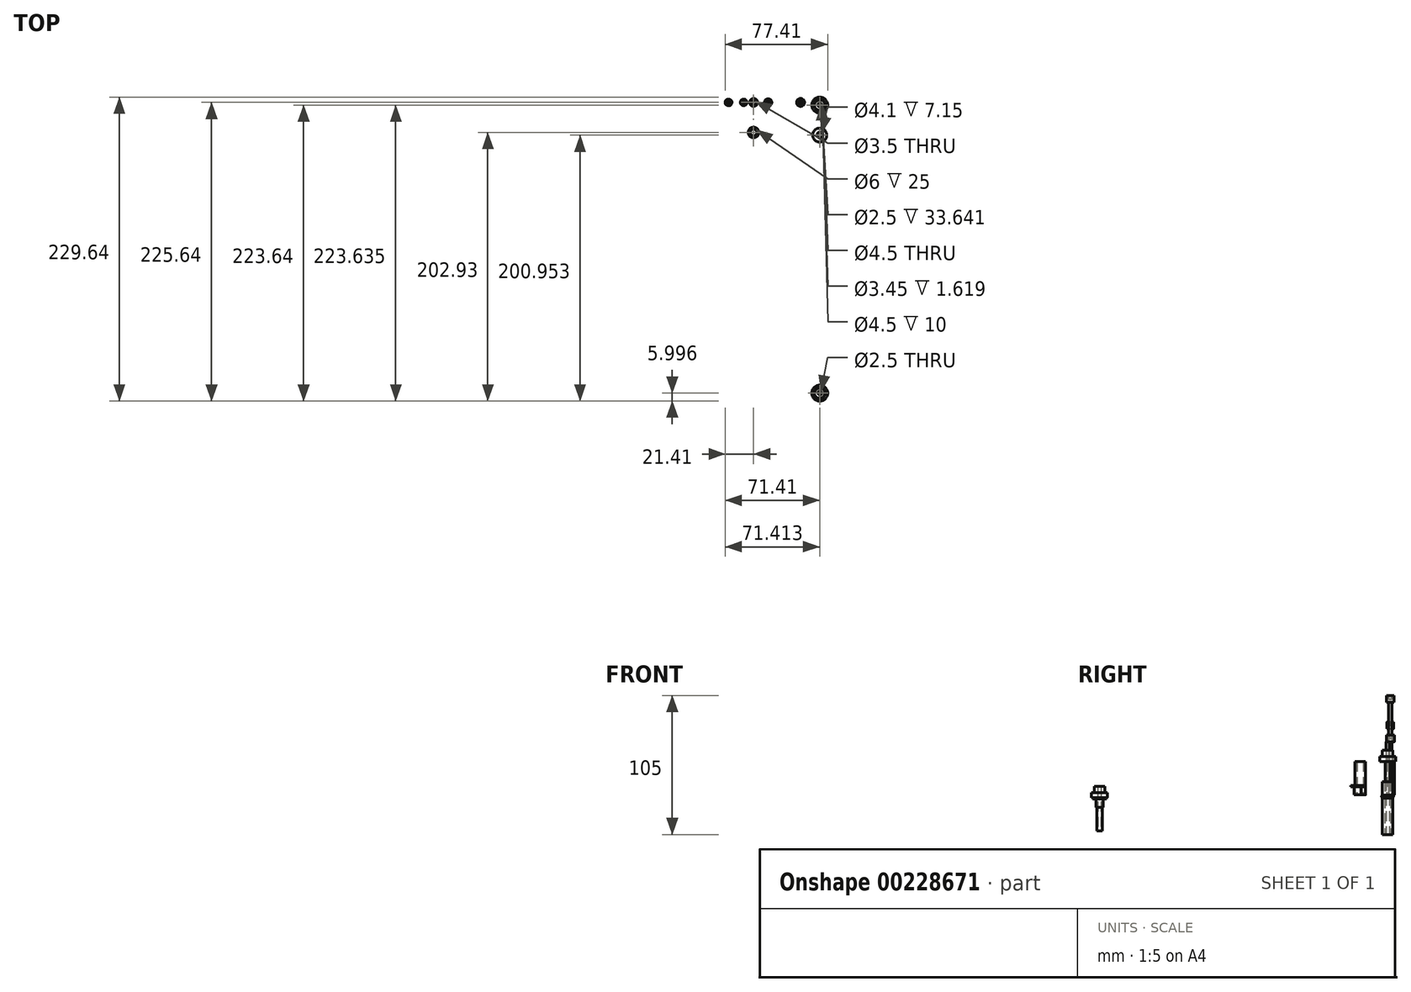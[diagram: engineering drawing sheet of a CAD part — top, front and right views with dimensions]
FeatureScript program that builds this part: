
annotation { "Feature Type Name" : "Feature", "Feature Type Description" : "" }
export const myFeature = defineFeature(function(context is Context, id is Id, definition is map)
    precondition{}
    {
        {
            var Q0;
            Q0=qCreatedBy(makeId("Top.planeOp"),FACE);
            var sketch = newSketch(context, id + "F0", { "sketchPlane" : qUnion([Q0])});
            skCircle(sketch, "E0", {"center": v(0, 0) * mm, "radius": 1.75 * mm});
            skCircle(sketch, "E1", {"center": v(0, 0) * mm, "radius": 3 * mm});
            skSolve(sketch);
        }
        {
            var Q0;
            Q0=makeQuery(id+"F0.imprint","IMPRINT",FACE,{"disambiguationData":[TD([[makeQuery(id+"F0.imprint","IMPRINT",EDGE,{"derivedFrom":sQuery(id+"F0.wireOp",EDGE,"E0")}),-1.0]])]});
            extrude(context, id + "F1", {"entities" : qUnion([Q0]), "depth" : 25 * mm});
        }
        {
            var Q0;
            Q0=qCreatedBy(makeId("Top.planeOp"),FACE);
            var sketch = newSketch(context, id + "F2", { "sketchPlane" : qUnion([Q0])});
            skCircle(sketch, "E2", {"center": v(-18.9, 0) * mm, "radius": 1 * mm});
            skSolve(sketch);
        }
        {
            var Q0;
            Q0=makeQuery(id+"F2.imprint","IMPRINT",FACE,{"disambiguationData":[TD([[makeQuery(id+"F2.imprint","IMPRINT",EDGE,{"derivedFrom":sQuery(id+"F2.wireOp",EDGE,"E2")}),1.0]])]});
            extrude(context, id + "F3", {"entities" : qUnion([Q0]), "depth" : 25 * mm});
        }
        {
            var Q0;
            Q0=qCreatedBy(makeId("Front.planeOp"),FACE);
            var sketch = newSketch(context, id + "F4", { "sketchPlane" : qUnion([Q0])});
            skArc(sketch, "E3", {"start": v(-18.9, 29) * mm, "mid": v(-21.4, 26.5) * mm, "end": v(-18.9, 24) * mm});
            skLineSegment(sketch, "E4.bottom", {"start": v(-19.9, 19.96) * mm, "end": v(-17.9, 19.96) * mm});
            skLineSegment(sketch, "E4.top", {"start": v(-19.9, 22.2) * mm, "end": v(-17.9, 22.2) * mm});
            skLineSegment(sketch, "E4.left", {"start": v(-19.9, 19.96) * mm, "end": v(-19.9, 22.2) * mm});
            skLineSegment(sketch, "E4.right", {"start": v(-17.9, 19.96) * mm, "end": v(-17.9, 22.2) * mm});
            skLineSegment(sketch, "E5", {"start": v(-18.9, 19.96) * mm, "end": v(-18.9, 30.05) * mm});
            skSolve(sketch);
        }
        {
            var Q0;
            {var subQ0=sQuery(id+"F4.wireOp",EDGE,"E3");Q0=makeQuery(id+"F4.imprint","IMPRINT",FACE,{"disambiguationData":[TD([[makeQuery(id+"F4.imprint","IMPRINT",EDGE,{"derivedFrom":subQ0}),1.0]])]});}
            var Q1;
            Q1=sQuery(id+"F4.wireOp",EDGE,"E3");
            var Q2;
            Q2=sQuery(id+"F4.wireOp",EDGE,"E5");
            revolve(context, id + "F5", {"operationType" : NewBodyOperationType.ADD, "entities" : qUnion([Q0]), "surfaceEntities" : qUnion([Q1]), "axis" : qUnion([Q2]), "revolveType" : RevolveType.FULL});
        }
        {
            var Q0;
            Q0=qCreatedBy(makeId("Top.planeOp"),FACE);
            var sketch = newSketch(context, id + "F6", { "sketchPlane" : qUnion([Q0])});
            skCircle(sketch, "E6", {"center": v(10.98, 0) * mm, "radius": 1.25 * mm});
            skSolve(sketch);
        }
        {
            var Q0;
            Q0=makeQuery(id+"F6.imprint","IMPRINT",FACE,{"disambiguationData":[TD([[makeQuery(id+"F6.imprint","IMPRINT",EDGE,{"derivedFrom":sQuery(id+"F6.wireOp",EDGE,"E6")}),1.0]])]});
            extrude(context, id + "F7", {"entities" : qUnion([Q0]), "depth" : 70 * mm});
        }
        {
            var Q0;
            Q0=qCreatedBy(makeId("Right.planeOp"),FACE);
            cPlane(context, id + "F8", {"entities" : qUnion([Q0]), "cplaneType" : CPlaneType.OFFSET, "offset" : 50 * mm, "width" : 150 * mm, "height" : 150 * mm});
        }
        {
            var Q0;
            Q0=qCreatedBy(id+"F8.planeOp",FACE);
            var sketch = newSketch(context, id + "F9", { "sketchPlane" : qUnion([Q0])});
            skLineSegment(sketch, "E7.bottom", {"start": v(0, 0) * mm, "end": v(-2, 0) * mm});
            skLineSegment(sketch, "E7.left", {"start": v(0, 0) * mm, "end": v(0, 25) * mm});
            skLineSegment(sketch, "E7.right", {"start": v(-4, 0) * mm, "end": v(-4, 25) * mm});
            skLineSegment(sketch, "E8.bottom", {"start": v(-8, 25) * mm, "end": v(-4, 25) * mm});
            skLineSegment(sketch, "E8.top", {"start": v(-8, 28.97) * mm, "end": v(-6, 28.97) * mm});
            skLineSegment(sketch, "E8.left", {"start": v(-8, 25) * mm, "end": v(-8, 28.97) * mm});
            skLineSegment(sketch, "E8.right", {"start": v(4, 25) * mm, "end": v(4, 28.97) * mm});
            skLineSegment(sketch, "E9.bottom", {"start": v(-6, 33.64) * mm, "end": v(-3.25, 33.64) * mm});
            skLineSegment(sketch, "E9.left", {"start": v(-6, 33.64) * mm, "end": v(-6, 28.97) * mm});
            skLineSegment(sketch, "E9.right", {"start": v(2, 33.64) * mm, "end": v(2, 28.97) * mm});
            skLineSegment(sketch, "E10.trimOffspring", {"start": v(2, 28.97) * mm, "end": v(4, 28.97) * mm});
            skPoint(sketch, "E11.start.orphan", {"position": v(-2, 0) * mm});
            skLineSegment(sketch, "E12.trimOffspring", {"start": v(0, 25) * mm, "end": v(4, 25) * mm});
            skLineSegment(sketch, "E13.left", {"start": v(-0.75, 33.64) * mm, "end": v(-0.75, 0) * mm});
            skLineSegment(sketch, "E13.right", {"start": v(-3.25, 33.64) * mm, "end": v(-3.25, 0) * mm});
            skPoint(sketch, "E13.bottom.end.orphan", {"position": v(-3.25, 38.46) * mm});
            skPoint(sketch, "E14.orphan", {"position": v(-0.75, 38.46) * mm});
            skLineSegment(sketch, "E15.trimOffspring", {"start": v(-0.75, 33.64) * mm, "end": v(2, 33.64) * mm});
            skLineSegment(sketch, "E16.trimOffspring", {"start": v(-3.25, 0) * mm, "end": v(-4, 0) * mm});
            skPoint(sketch, "E13.top.end.orphan", {"position": v(-3.25, -38.46) * mm});
            skPoint(sketch, "E13.top.start.orphan", {"position": v(-0.75, -38.46) * mm});
            skLineSegment(sketch, "E17", {"start": v(-2, 0) * mm, "end": v(-2, 45.17) * mm});
            skSolve(sketch);
        }
        {
            var Q0;
            Q0=makeQuery(id+"F9.imprint","IMPRINT",FACE,{"disambiguationData":[TD([[makeQuery(id+"F9.imprint","IMPRINT",EDGE,{"derivedFrom":sQuery(id+"F9.wireOp",EDGE,"E7.right")}),-1.0]])]});
            var Q1;
            Q1=sQuery(id+"F9.wireOp",EDGE,"E17");
            revolve(context, id + "F10", {"entities" : qUnion([Q0]), "axis" : qUnion([Q1]), "revolveType" : RevolveType.FULL});
        }
        {
            var Q0;
            Q0=qCreatedBy(id+"F8.planeOp",FACE);
            var sketch = newSketch(context, id + "F11", { "sketchPlane" : qUnion([Q0])});
            skLineSegment(sketch, "E18", {"start": v(-24.69, 22.6) * mm, "end": v(-24.69, -20.78) * mm});
            skLineSegment(sketch, "E19.bottom", {"start": v(-27.34, 0) * mm, "end": v(-26.74, 0) * mm});
            skLineSegment(sketch, "E19.left", {"start": v(-27.34, 0) * mm, "end": v(-27.34, 6.15) * mm});
            skLineSegment(sketch, "E19.right", {"start": v(-22.04, 0) * mm, "end": v(-22.04, 6.15) * mm});
            skPoint(sketch, "E19.middle", {"position": v(-24.69, 3.08) * mm});
            skLineSegment(sketch, "E20.bottom", {"start": v(-29.99, 6.15) * mm, "end": v(-27.34, 6.15) * mm});
            skLineSegment(sketch, "E20.top", {"start": v(-29.99, 7.15) * mm, "end": v(-26.74, 7.15) * mm});
            skLineSegment(sketch, "E20.left", {"start": v(-29.99, 6.15) * mm, "end": v(-29.99, 7.15) * mm});
            skLineSegment(sketch, "E20.right", {"start": v(-19.39, 6.15) * mm, "end": v(-19.39, 7.15) * mm});
            skLineSegment(sketch, "E21.trimOffspring", {"start": v(-22.04, 6.15) * mm, "end": v(-19.39, 6.15) * mm});
            skLineSegment(sketch, "E22.left", {"start": v(-26.74, 0) * mm, "end": v(-26.74, 7.15) * mm});
            skLineSegment(sketch, "E22.right", {"start": v(-22.64, 0) * mm, "end": v(-22.64, 7.15) * mm});
            skLineSegment(sketch, "E23.trimOffspring", {"start": v(-22.64, 0) * mm, "end": v(-22.04, 0) * mm});
            skLineSegment(sketch, "E24.trimOffspring", {"start": v(-22.64, 7.15) * mm, "end": v(-19.39, 7.15) * mm});
            skPoint(sketch, "E22.top.start.orphan", {"position": v(-26.74, 26.34) * mm});
            skPoint(sketch, "E25.orphan", {"position": v(-22.64, 26.34) * mm});
            skPoint(sketch, "E26.orphan", {"position": v(-22.64, -20.19) * mm});
            skPoint(sketch, "E22.bottom.start.orphan", {"position": v(-26.74, -20.19) * mm});
            skSolve(sketch);
        }
        {
            var Q0;
            Q0=makeQuery(id+"F11.imprint","IMPRINT",FACE,{"disambiguationData":[TD([[makeQuery(id+"F11.imprint","IMPRINT",EDGE,{"derivedFrom":sQuery(id+"F11.wireOp",EDGE,"E19.bottom")}),1.0]])]});
            var Q1;
            Q1=sQuery(id+"F11.wireOp",EDGE,"E18");
            revolve(context, id + "F12", {"entities" : qUnion([Q0]), "axis" : qUnion([Q1]), "revolveType" : RevolveType.FULL});
        }
        {
            var Q0;
            Q0=qCreatedBy(id+"F8.planeOp",FACE);
            var sketch = newSketch(context, id + "F13", { "sketchPlane" : qUnion([Q0])});
            skLineSegment(sketch, "E27.bottom", {"start": v(-217.64, -27.28) * mm, "end": v(-219.64, -27.28) * mm});
            skLineSegment(sketch, "E27.left", {"start": v(-217.64, -27.28) * mm, "end": v(-217.64, -2.28) * mm});
            skLineSegment(sketch, "E27.right", {"start": v(-221.64, -27.28) * mm, "end": v(-221.64, -9.43) * mm});
            skLineSegment(sketch, "E28.bottom", {"start": v(-225.64, -2.28) * mm, "end": v(-224.94, -2.28) * mm});
            skLineSegment(sketch, "E28.top", {"start": v(-225.64, 1.7) * mm, "end": v(-223.64, 1.7) * mm});
            skLineSegment(sketch, "E28.left", {"start": v(-225.64, -2.28) * mm, "end": v(-225.64, 1.7) * mm});
            skLineSegment(sketch, "E28.right", {"start": v(-213.64, -2.28) * mm, "end": v(-213.64, 1.7) * mm});
            skLineSegment(sketch, "E29.bottom", {"start": v(-223.64, 6.37) * mm, "end": v(-220.9, 6.37) * mm});
            skLineSegment(sketch, "E29.left", {"start": v(-223.64, 6.37) * mm, "end": v(-223.64, 1.7) * mm});
            skLineSegment(sketch, "E29.right", {"start": v(-215.64, 6.37) * mm, "end": v(-215.64, 1.7) * mm});
            skLineSegment(sketch, "E30.trimOffspring", {"start": v(-215.64, 1.7) * mm, "end": v(-213.64, 1.7) * mm});
            skPoint(sketch, "E31.start.orphan", {"position": v(-219.64, -27.28) * mm});
            skLineSegment(sketch, "E32.trimOffspring", {"start": v(-217.64, -2.28) * mm, "end": v(-213.64, -2.28) * mm});
            skLineSegment(sketch, "E33.left", {"start": v(-218.4, 6.37) * mm, "end": v(-218.4, -27.28) * mm});
            skLineSegment(sketch, "E33.right", {"start": v(-220.9, 6.37) * mm, "end": v(-220.9, -27.28) * mm});
            skPoint(sketch, "E33.bottom.end.orphan", {"position": v(-220.9, 11.19) * mm});
            skPoint(sketch, "E34.orphan", {"position": v(-218.4, 11.19) * mm});
            skLineSegment(sketch, "E35.trimOffspring", {"start": v(-218.4, 6.37) * mm, "end": v(-215.64, 6.37) * mm});
            skLineSegment(sketch, "E36.trimOffspring", {"start": v(-220.9, -27.28) * mm, "end": v(-221.64, -27.28) * mm});
            skLineSegment(sketch, "E37", {"start": v(-219.64, -27.28) * mm, "end": v(-219.64, 78.9) * mm});
            skLineSegment(sketch, "E38", {"start": v(-219.64, 13.18) * mm, "end": v(-219.64, -30.2) * mm});
            skLineSegment(sketch, "E39.bottom", {"start": v(-222.3, -9.43) * mm, "end": v(-221.64, -9.43) * mm});
            skLineSegment(sketch, "E39.left", {"start": v(-222.3, -9.43) * mm, "end": v(-222.3, -3.28) * mm});
            skLineSegment(sketch, "E39.right", {"start": v(-217, -9.43) * mm, "end": v(-217, -3.28) * mm});
            skPoint(sketch, "E39.middle", {"position": v(-219.64, -6.35) * mm});
            skLineSegment(sketch, "E40.bottom", {"start": v(-224.94, -3.28) * mm, "end": v(-222.3, -3.28) * mm});
            skLineSegment(sketch, "E40.left", {"start": v(-224.94, -3.28) * mm, "end": v(-224.94, -2.28) * mm});
            skLineSegment(sketch, "E40.right", {"start": v(-214.34, -3.28) * mm, "end": v(-214.34, -2.28) * mm});
            skLineSegment(sketch, "E41.trimOffspring", {"start": v(-217, -3.28) * mm, "end": v(-214.34, -3.28) * mm});
            skLineSegment(sketch, "E42.right", {"start": v(-217.6, -9.43) * mm, "end": v(-217.6, -2.28) * mm});
            skLineSegment(sketch, "E43.trimOffspring", {"start": v(-217.6, -9.43) * mm, "end": v(-217, -9.43) * mm});
            skLineSegment(sketch, "E44.trimOffspring", {"start": v(-217.6, -2.28) * mm, "end": v(-214.34, -2.28) * mm});
            skPoint(sketch, "E42.top.start.orphan", {"position": v(-221.7, 16.91) * mm});
            skPoint(sketch, "E45.orphan", {"position": v(-217.6, 16.91) * mm});
            skPoint(sketch, "E46.orphan", {"position": v(-217.6, -29.61) * mm});
            skPoint(sketch, "E42.bottom.start.orphan", {"position": v(-221.7, -29.61) * mm});
            skLineSegment(sketch, "E47.trimOffspring", {"start": v(-221.7, -2.28) * mm, "end": v(-221.64, -2.28) * mm});
            skSolve(sketch);
        }
        {
            var Q0;
            Q0=makeQuery(id+"F13.imprint","IMPRINT",FACE,{"disambiguationData":[TD([[makeQuery(id+"F13.imprint","IMPRINT",EDGE,{"derivedFrom":sQuery(id+"F13.wireOp",EDGE,"E27.right")}),-1.0]])]});
            var Q1;
            Q1=sQuery(id+"F13.wireOp",EDGE,"E37");
            revolve(context, id + "F14", {"entities" : qUnion([Q0]), "axis" : qUnion([Q1]), "revolveType" : RevolveType.FULL});
        }
        {
            var Q0;
            Q0=makeQuery(id+"F7.opExtrude","CAP_FACE",FACE,{"disambiguationData":[OSD([sQuery(id+"F6.wireOp",EDGE,"E6")])],"isStart":false});
            var sketch = newSketch(context, id + "F15", { "sketchPlane" : qUnion([Q0])});
            skCircle(sketch, "E48", {"center": v(10.98, 0) * mm, "radius": 2.8 * mm});
            skSolve(sketch);
        }
        {
            var Q0;
            Q0=makeQuery(id+"F15.imprint","IMPRINT",FACE,{"disambiguationData":[TD([[makeQuery(id+"F15.imprint","IMPRINT",EDGE,{"derivedFrom":sQuery(id+"F15.wireOp",EDGE,"E48")}),1.0]])]});
            var Q1;
            Q1=makeQuery(id+"F15.imprint","IMPRINT",FACE,{"disambiguationData":[TD([[makeQuery(id+"F15.imprint","IMPRINT",EDGE,{"derivedFrom":makeQuery(id+"F7.opExtrude","CAP_EDGE",EDGE,{"disambiguationData":[OSD([sQuery(id+"F6.wireOp",EDGE,"E6")])],"isStart":false})}),1.0]])]});
            extrude(context, id + "F16", {"entities" : qUnion([Q0, Q1]), "operationType" : NewBodyOperationType.ADD, "depth" : 5 * mm});
        }
        {
            var Q0;
            Q0=makeQuery(id+"F16.opExtrude","CAP_FACE",FACE,{"disambiguationData":[OSD([sQuery(id+"F15.wireOp",EDGE,"E48")])],"isStart":false});
            var sketch = newSketch(context, id + "F17", { "sketchPlane" : qUnion([Q0])});
            skText(sketch, "E49", { "text": "70\n", "fontName": "OpenSans-Regular.ttf"});
            const initialGuessF17  = {"E49": [0.009, -0.0012, 1, 0, 0.00249]};
            skSetInitialGuess(sketch, initialGuessF17);
            skSolve(sketch);
        }
        {
            var Q0;
            Q0 = qSketchRegion(id + "F17", true);
            extrude(context, id + "F18", {"entities" : qUnion([Q0]), "operationType" : NewBodyOperationType.REMOVE, "oppositeDirection" : true, "depth" : 3 * mm});
        }
        {
            var Q0;
            Q0=qCreatedBy(makeId("Top.planeOp"),FACE);
            var sketch = newSketch(context, id + "F19", { "sketchPlane" : qUnion([Q0])});
            skCircle(sketch, "E50", {"center": v(-7.47, 0) * mm, "radius": 1.25 * mm});
            skSolve(sketch);
        }
        {
            var Q0;
            Q0=makeQuery(id+"F19.imprint","IMPRINT",FACE,{"disambiguationData":[TD([[makeQuery(id+"F19.imprint","IMPRINT",EDGE,{"derivedFrom":sQuery(id+"F19.wireOp",EDGE,"E50")}),1.0]])]});
            extrude(context, id + "F20", {"entities" : qUnion([Q0]), "depth" : 50 * mm});
        }
        {
            var Q0;
            Q0=makeQuery(id+"F20.opExtrude","CAP_FACE",FACE,{"disambiguationData":[OSD([sQuery(id+"F19.wireOp",EDGE,"E50")])],"isStart":false});
            var sketch = newSketch(context, id + "F21", { "sketchPlane" : qUnion([Q0])});
            skCircle(sketch, "E51", {"center": v(-7.47, 0) * mm, "radius": 2.5 * mm});
            skSolve(sketch);
        }
        {
            var Q0;
            Q0=makeQuery(id+"F21.imprint","IMPRINT",FACE,{"disambiguationData":[TD([[makeQuery(id+"F21.imprint","IMPRINT",EDGE,{"derivedFrom":makeQuery(id+"F20.opExtrude","CAP_EDGE",EDGE,{"disambiguationData":[OSD([sQuery(id+"F19.wireOp",EDGE,"E50")])],"isStart":false})}),1.0]])]});
            var Q1;
            Q1=makeQuery(id+"F21.imprint","IMPRINT",FACE,{"disambiguationData":[TD([[makeQuery(id+"F21.imprint","IMPRINT",EDGE,{"derivedFrom":sQuery(id+"F21.wireOp",EDGE,"E51")}),1.0]])]});
            extrude(context, id + "F22", {"entities" : qUnion([Q0, Q1]), "operationType" : NewBodyOperationType.ADD, "depth" : 5 * mm});
        }
        {
            var Q0;
            Q0=makeQuery(id+"F22.opExtrude","CAP_FACE",FACE,{"disambiguationData":[OSD([sQuery(id+"F21.wireOp",EDGE,"E51")])],"isStart":false});
            var sketch = newSketch(context, id + "F23", { "sketchPlane" : qUnion([Q0])});
            skText(sketch, "E52", { "text": "50", "fontName": "OpenSans-Regular.ttf"});
            const initialGuessF23  = {"E52": [-0.00932, -0.00168, 1, 0, 0.0023]};
            skSetInitialGuess(sketch, initialGuessF23);
            skSolve(sketch);
        }
        {
            var Q0;
            Q0 = qSketchRegion(id + "F23", true);
            extrude(context, id + "F24", {"entities" : qUnion([Q0]), "operationType" : NewBodyOperationType.REMOVE, "oppositeDirection" : true, "depth" : 2.5 * mm});
        }
        {
            var Q0;
            Q0=qCreatedBy(makeId("Top.planeOp"),FACE);
            var sketch = newSketch(context, id + "F25", { "sketchPlane" : qUnion([Q0])});
            skCircle(sketch, "E53", {"center": v(35.5, 0) * mm, "radius": 1.25 * mm});
            skSolve(sketch);
        }
        {
            var Q0;
            Q0=makeQuery(id+"F25.imprint","IMPRINT",FACE,{"disambiguationData":[TD([[makeQuery(id+"F25.imprint","IMPRINT",EDGE,{"derivedFrom":sQuery(id+"F25.wireOp",EDGE,"E53")}),1.0]])]});
            extrude(context, id + "F26", {"entities" : qUnion([Q0]), "depth" : 40 * mm});
        }
        {
            var Q0;
            Q0=makeQuery(id+"F26.opExtrude","CAP_FACE",FACE,{"disambiguationData":[OSD([sQuery(id+"F25.wireOp",EDGE,"E53")])],"isStart":false});
            var sketch = newSketch(context, id + "F27", { "sketchPlane" : qUnion([Q0])});
            skCircle(sketch, "E54", {"center": v(35.5, 0) * mm, "radius": 3.02 * mm});
            skSolve(sketch);
        }
        {
            var Q0;
            Q0=makeQuery(id+"F27.imprint","IMPRINT",FACE,{"disambiguationData":[TD([[makeQuery(id+"F27.imprint","IMPRINT",EDGE,{"derivedFrom":makeQuery(id+"F26.opExtrude","CAP_EDGE",EDGE,{"disambiguationData":[OSD([sQuery(id+"F25.wireOp",EDGE,"E53")])],"isStart":false})}),1.0]])]});
            var Q1;
            Q1=makeQuery(id+"F27.imprint","IMPRINT",FACE,{"disambiguationData":[TD([[makeQuery(id+"F27.imprint","IMPRINT",EDGE,{"derivedFrom":sQuery(id+"F27.wireOp",EDGE,"E54")}),1.0]])]});
            extrude(context, id + "F28", {"entities" : qUnion([Q0, Q1]), "operationType" : NewBodyOperationType.ADD, "depth" : 5 * mm});
        }
        {
            var Q0;
            Q0=makeQuery(id+"F28.opExtrude","CAP_FACE",FACE,{"disambiguationData":[OSD([sQuery(id+"F27.wireOp",EDGE,"E54")])],"isStart":false});
            var sketch = newSketch(context, id + "F29", { "sketchPlane" : qUnion([Q0])});
            skText(sketch, "E55", { "text": "40", "fontName": "OpenSans-Regular.ttf"});
            const initialGuessF29  = {"E55": [0.03295, -0.00156, 1, 0, 0.00319]};
            skSetInitialGuess(sketch, initialGuessF29);
            skSolve(sketch);
        }
        {
            var Q0;
            Q0 = qSketchRegion(id + "F29", true);
            extrude(context, id + "F30", {"entities" : qUnion([Q0]), "operationType" : NewBodyOperationType.REMOVE, "oppositeDirection" : true, "depth" : 2.5 * mm});
        }
        {
            var Q0;
            Q0=qCreatedBy(makeId("Top.planeOp"),FACE);
            var sketch = newSketch(context, id + "F31", { "sketchPlane" : qUnion([Q0])});
            skCircle(sketch, "E56", {"center": v(0, -22.71) * mm, "radius": 4 * mm});
            skCircle(sketch, "E57", {"center": v(0, -22.71) * mm, "radius": 3 * mm});
            skCircle(sketch, "E58", {"center": v(0, -22.71) * mm, "radius": 2.5 * mm});
            skSolve(sketch);
        }
        {
            var Q0;
            Q0=makeQuery(id+"F31.imprint","IMPRINT",FACE,{"disambiguationData":[TD([[makeQuery(id+"F31.imprint","IMPRINT",EDGE,{"derivedFrom":sQuery(id+"F31.wireOp",EDGE,"E58")}),1.0]])]});
            var Q1;
            Q1=makeQuery(id+"F31.imprint","IMPRINT",FACE,{"disambiguationData":[TD([[makeQuery(id+"F31.imprint","IMPRINT",EDGE,{"derivedFrom":sQuery(id+"F31.wireOp",EDGE,"E56")}),1.0]])]});
            extrude(context, id + "F32", {"entities" : qUnion([Q0, Q1]), "depth" : 25 * mm});
        }
        {
            var Q0;
            Q0=qCreatedBy(makeId("Top.planeOp"),FACE);
            var sketch = newSketch(context, id + "F33", { "sketchPlane" : qUnion([Q0])});
            skCircle(sketch, "E59", {"center": v(50, -2) * mm, "radius": 2.25 * mm});
            skCircle(sketch, "E60", {"center": v(50, -2) * mm, "radius": 4 * mm});
            skSolve(sketch);
        }
        {
            var Q0;
            Q0=makeQuery(id+"F33.imprint","IMPRINT",FACE,{"disambiguationData":[TD([[makeQuery(id+"F33.imprint","IMPRINT",EDGE,{"derivedFrom":sQuery(id+"F33.wireOp",EDGE,"E59")}),-1.0]])]});
            extrude(context, id + "F34", {"entities" : qUnion([Q0]), "depth" : 10 * mm});
        }
        {
            var Q0;
            Q0 = qSketchRegion(id + "F33", true);
            extrude(context, id + "F35", {"entities" : qUnion([Q0]), "operationType" : NewBodyOperationType.ADD, "oppositeDirection" : true, "depth" : 30 * mm});
        }
        {
            var Q0;
            Q0=makeQuery(id+"F35.opExtrude","CAP_FACE",FACE,{"disambiguationData":[OSD([sQuery(id+"F33.wireOp",EDGE,"E59"),sQuery(id+"F33.wireOp",EDGE,"E60")])],"isStart":false});
            var sketch = newSketch(context, id + "F36", { "sketchPlane" : qUnion([Q0])});
            skCircle(sketch, "E61", {"center": v(50, 2) * mm, "radius": 1.25 * mm});
            skSolve(sketch);
        }
        {
            var Q0;
            Q0=makeQuery(id+"F36.imprint","IMPRINT",FACE,{"disambiguationData":[TD([[makeQuery(id+"F36.imprint","IMPRINT",EDGE,{"derivedFrom":sQuery(id+"F36.wireOp",EDGE,"E61")}),1.0]])]});
            extrude(context, id + "F37", {"entities" : qUnion([Q0]), "oppositeDirection" : true, "depth" : 70 * mm});
        }
        {
            var Q0;
            Q0=qCreatedBy(makeId("Top.planeOp"),FACE);
            var sketch = newSketch(context, id + "F38", { "sketchPlane" : qUnion([Q0])});
            skCircle(sketch, "E62", {"center": v(50, -2) * mm, "radius": 4.65 * mm});
            skCircle(sketch, "E63", {"center": v(50, -2) * mm, "radius": 1.72 * mm});
            skSolve(sketch);
        }
        {
            var Q0;
            Q0=makeQuery(id+"F38.imprint","IMPRINT",FACE,{"disambiguationData":[TD([[makeQuery(id+"F38.imprint","IMPRINT",EDGE,{"derivedFrom":sQuery(id+"F38.wireOp",EDGE,"E62")}),1.0]])]});
            extrude(context, id + "F39", {"entities" : qUnion([Q0]), "operationType" : NewBodyOperationType.ADD, "oppositeDirection" : true, "depth" : 2.5 * mm});
        }
        {
            var Q0;
            Q0=makeQuery(id+"F39.opExtrude","CAP_EDGE",EDGE,{"disambiguationData":[OSD([sQuery(id+"F38.wireOp",EDGE,"E62")])],"isStart":false});
            var Q1;
            Q1=makeQuery(id+"F39.opExtrude","CAP_EDGE",EDGE,{"disambiguationData":[OSD([sQuery(id+"F38.wireOp",EDGE,"E62")])],"isStart":true});
            chamfer(context, id + "F40", {"entities" : qUnion([Q0, Q1]), "width" : 0.8 * mm, "tangentPropagation" : true});
        }
        {
            var Q0;
            Q0=makeQuery(id+"F39.opExtrude","CAP_EDGE",EDGE,{"disambiguationData":[OSD([sQuery(id+"F38.wireOp",EDGE,"E63")])],"isStart":false});
            fillet(context, id + "F41", {"entities" : qUnion([Q0]), "radius" : 1 * mm, "tangentPropagation" : true, "allowEdgeOverflow" : false});
        }
    });
